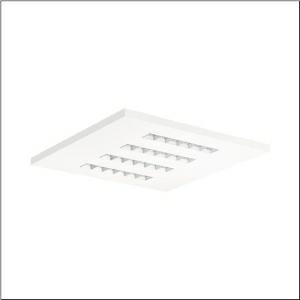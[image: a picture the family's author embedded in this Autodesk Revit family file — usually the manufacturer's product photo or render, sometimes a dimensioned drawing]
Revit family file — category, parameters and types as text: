
# Revit family: silica_r__21_square_51mx6mdu34w_1727
name_source: partatom
category: Lighting Fixtures
units: mm (PartAtom-declared; Revit-internal decimal feet)

## family parameters
Cut with Voids When Loaded = No
Host = Face
Light Source = No
Part Type = Normal
Room Calculation Point = No
Round Connector Dimension = Use Diameter
Shared = No

## types (1)
- --- (1 x LED, 4600 lm, 29.2 W, 3000K)
    Apparent Load = 29 VA
    CIE Flux Codes = 83 98 100 100 100
    Color Rendering = 80
    Color Temperature = 3000K
    Default Elevation = 1800 mm
    Description = Silica® 21 Square, office luminaire, primary light control with lens, of PMMA, primary anti-glare with reflector, of PC, white, CAT 2 (L<= 3000cd/m²), light emission: direct distribution, primary light characteristic: symmetric, installation type: lay-in mounting, LED, rated luminous flux: 4.600lm, luminous efficacy: 158lm/W, light colour: 830, colour temperature: 3000K, control gear: DALI 2, with terminal, 5-pole, mains connection: 220..240V, AC, 50/60Hz, rated input power: 29.2W, luminaire housing, of sheet steel, coated, traffic white (RAL 9016), module: M625, length: 622mm, width: 622mm, height: 33mm, protection rating (complete): IP20, insulation class (complete): insulation class I (protective earthing), certification: CE, ENEC, VDE, permissible operating ambient temperature: -20..+40°C, standard: EN 50419, packaging unit: 1 piece
    Height = 0 mm  [stored 0 ft]
    Lamp = 1 x LED
    Lamp Light Flux = 4600 lm
    Lamp Power = 29.2 W
    Lamp count = 1
    Length = 622 mm
    Luminous efficacy = 158 lm/W
    Manufacturer = Siteco
    ModVariant = No
    Model = 51MX6MDU34W
    Mounting Place = Ceiling
    Mounting Type = Recessed
    Number of Poles = 1
    OnlyDefault = Yes
    Power Factor = 1
    Product Name = Silica® 21 Square
    Product group = office luminaire | ceiling recessed
    ProductGroupID = 400
    Protection Class = Protection class I
    Protection Degree = IP 20
    RLX_Detail_Level = 1
    RLX_Emergency_Light_Flux = 0 lm
    RLX_Emergency_Type = 0
    RLX_Emergency_Type_DB = No
    RlxData = <blob elided: 18533 chars, md5=34fe8e34>
    Socket = socket
    Standby Power = 0 W
    System Light Flux = 4600 lm
    System Power = 29 W
    Type Comments = factory setting: luminous flux: 100 % | dim-lin: 254 | 393 mA
    Type Image = l_1275220.jpg
    URL = http://relux.com
    VarID = @adj_105257
    Voltage = 0 V
    Weight = 0.00 kg
    Width = 622 mm

note: [stored X ft] marks values corroborated as IEEE doubles in the binary element streams (Revit-internal decimal feet)

## geometry (parser evidence)
native form markers: Blend x4, Sweep x13
no freeform markers — native parametric forms only
